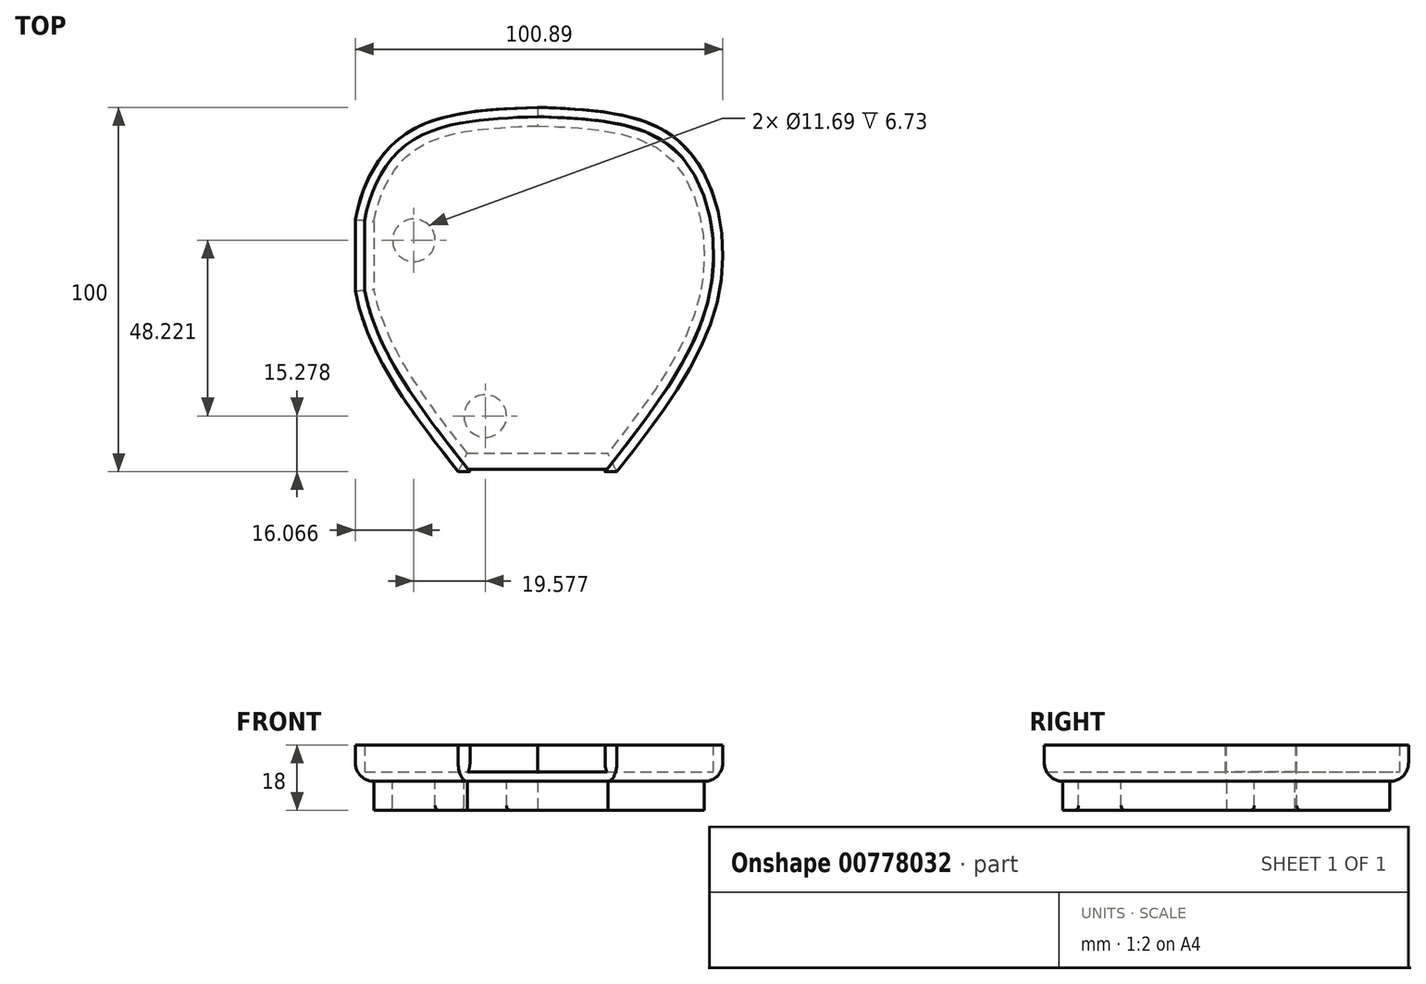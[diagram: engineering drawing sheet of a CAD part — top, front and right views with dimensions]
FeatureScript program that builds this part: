
annotation { "Feature Type Name" : "Feature", "Feature Type Description" : "" }
export const myFeature = defineFeature(function(context is Context, id is Id, definition is map)
    precondition{}
    {
        {
            var Q0;
            Q0=qCreatedBy(makeId("Top.planeOp"),FACE);
            var sketch = newSketch(context, id + "F0", { "sketchPlane" : qUnion([Q0])});
            skLineSegment(sketch, "E0", {"start": v(0, 50.38) * mm, "end": v(-50, 50.38) * mm});
            skLineSegment(sketch, "E1", {"start": v(-50, 50.38) * mm, "end": v(-50, -49.62) * mm});
            skLineSegment(sketch, "E2", {"start": v(-21.78, -49.62) * mm, "end": v(0, -49.62) * mm});
            skPoint(sketch, "E3.1.internal.snap0", {"position": v(-50, 0.38) * mm});
            skFitSpline(sketch, "E3", {"points": [v(-21.78, -49.62) * mm, v(-50, 0) * mm, v(-39.15, 40.83) * mm, v(0, 50.38) * mm], "startDerivative": vector(-101.07, 128.62) * mm, "endDerivative": vector(143.23, 5.45) * mm});
            skLineSegment(sketch, "E4", {"start": v(0, 0) * mm, "end": v(0, 24.08) * mm});
            skFitSpline(sketch, "E5.MirrorCS", {"points": [v(21.78, -49.62) * mm, v(50, 0) * mm, v(39.15, 40.83) * mm, v(0, 50.38) * mm], "startDerivative": vector(101.07, 128.62) * mm, "endDerivative": vector(-143.23, 5.45) * mm});
            skLineSegment(sketch, "E6.MirrorCS", {"start": v(21.78, -49.62) * mm, "end": v(0, -49.62) * mm});
            skSolve(sketch);
        }
        {
            var Q0;
            {var subQ4=sQuery(id+"F0.wireOp",EDGE,"E2");Q0=makeQuery(id+"F0.imprint","IMPRINT",FACE,{"disambiguationData":[TD([[makeQuery(id+"F0.imprint","IMPRINT",EDGE,{"derivedFrom":subQ4}),1.0]])]});}
            extrude(context, id + "F1", {"entities" : qUnion([Q0]), "depth" : 10 * mm, "offsetDistance" : 25.4 * mm});
        }
        {
            var Q0;
            Q0=makeQuery(id+"F1.opExtrude","CAP_FACE",FACE,{"disambiguationData":[OSD([sQuery(id+"F0.wireOp",EDGE,"E1"),sQuery(id+"F0.wireOp",EDGE,"E2"),sQuery(id+"F0.wireOp",EDGE,"E3"),sQuery(id+"F0.wireOp",EDGE,"E5.MirrorCS"),sQuery(id+"F0.wireOp",EDGE,"E6.MirrorCS")])],"isStart":false});
            var Q1;
            Q1=makeQuery(id+"F1.opExtrude","SWEPT_FACE",FACE,{"disambiguationData":[OSD([sQuery(id+"F0.wireOp",EDGE,"E2"),sQuery(id+"F0.wireOp",EDGE,"E6.MirrorCS")])]});
            shell(context, id + "F2", {"entities" : qUnion([Q0, Q1]), "thickness" : 2.54 * mm});
        }
        {
            var Q0;
            Q0=makeQuery(id+"F1.opExtrude","CAP_FACE",FACE,{"disambiguationData":[OSD([sQuery(id+"F0.wireOp",EDGE,"E1"),sQuery(id+"F0.wireOp",EDGE,"E2"),sQuery(id+"F0.wireOp",EDGE,"E3"),sQuery(id+"F0.wireOp",EDGE,"E5.MirrorCS"),sQuery(id+"F0.wireOp",EDGE,"E6.MirrorCS")])],"isStart":true});
            fillet(context, id + "F3", {"entities" : qUnion([Q0]), "radius" : 5.08 * mm, "tangentPropagation" : true, "allowEdgeOverflow" : false});
        }
        {
            var Q0;
            Q0=makeQuery(id+"F1.opExtrude","CAP_FACE",FACE,{"disambiguationData":[OSD([sQuery(id+"F0.wireOp",EDGE,"E1"),sQuery(id+"F0.wireOp",EDGE,"E2"),sQuery(id+"F0.wireOp",EDGE,"E3"),sQuery(id+"F0.wireOp",EDGE,"E5.MirrorCS"),sQuery(id+"F0.wireOp",EDGE,"E6.MirrorCS")])],"isStart":true});
            var sketch = newSketch(context, id + "F4", { "sketchPlane" : qUnion([Q0])});
            skLineSegment(sketch, "E7", {"start": v(0, 0) * mm, "end": v(0, 22.1) * mm});
            skCircle(sketch, "E8", {"center": v(14.36, 34.34) * mm, "radius": 5.85 * mm});
            skCircle(sketch, "E9", {"center": v(33.93, -13.88) * mm, "radius": 5.85 * mm});
            skCircle(sketch, "E10.MirrorC", {"center": v(-14.36, 34.34) * mm, "radius": 5.85 * mm});
            skCircle(sketch, "E11.MirrorC", {"center": v(-33.93, -13.88) * mm, "radius": 5.85 * mm});
            skSolve(sketch);
        }
        {
            var Q0;
            Q0=makeQuery(id+"F4.imprint","IMPRINT",FACE,{"disambiguationData":[TD([[makeQuery(id+"F4.imprint","IMPRINT",EDGE,{"derivedFrom":sQuery(id+"F4.wireOp",EDGE,"E9")}),1.0]])]});
            var Q1;
            Q1=makeQuery(id+"F4.imprint","IMPRINT",FACE,{"disambiguationData":[TD([[makeQuery(id+"F4.imprint","IMPRINT",EDGE,{"derivedFrom":sQuery(id+"F4.wireOp",EDGE,"E8")}),1.0]])]});
            var Q2;
            Q2=makeQuery(id+"F4.imprint","IMPRINT",FACE,{"disambiguationData":[TD([[makeQuery(id+"F4.imprint","IMPRINT",EDGE,{"derivedFrom":sQuery(id+"F4.wireOp",EDGE,"E10.MirrorC")}),-1.0]])]});
            var Q3;
            Q3=makeQuery(id+"F4.imprint","IMPRINT",FACE,{"disambiguationData":[TD([[makeQuery(id+"F4.imprint","IMPRINT",EDGE,{"derivedFrom":sQuery(id+"F4.wireOp",EDGE,"E11.MirrorC")}),-1.0]])]});
            extrude(context, id + "F5", {"entities" : qUnion([Q0, Q1, Q2, Q3]), "operationType" : NewBodyOperationType.ADD, "depth" : 8 * mm, "offsetDistance" : 25.4 * mm});
        }
        {
            var Q0;
            Q0=makeQuery(id+"F5.opExtrude","CAP_EDGE",EDGE,{"disambiguationData":[OSD([sQuery(id+"F4.wireOp",EDGE,"E9")])],"isStart":false});
            var Q1;
            Q1=makeQuery(id+"F5.opExtrude","CAP_EDGE",EDGE,{"disambiguationData":[OSD([sQuery(id+"F4.wireOp",EDGE,"E8")])],"isStart":false});
            var Q2;
            Q2=makeQuery(id+"F5.opExtrude","CAP_EDGE",EDGE,{"disambiguationData":[OSD([sQuery(id+"F4.wireOp",EDGE,"E10.MirrorC")])],"isStart":false});
            var Q3;
            Q3=makeQuery(id+"F5.opExtrude","CAP_EDGE",EDGE,{"disambiguationData":[OSD([sQuery(id+"F4.wireOp",EDGE,"E11.MirrorC")])],"isStart":false});
            fillet(context, id + "F6", {"entities" : qUnion([Q0, Q1, Q2, Q3]), "radius" : 1.27 * mm, "tangentPropagation" : true, "allowEdgeOverflow" : false});
        }
    });
